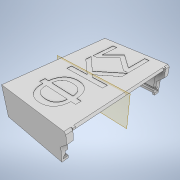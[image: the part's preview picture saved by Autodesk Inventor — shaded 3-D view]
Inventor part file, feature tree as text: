
AUTODESK INVENTOR PART (.ipt)
format: ipt  version: 2020.1 (Build 241239000, 239)  size: 393,728 bytes
history: native  units: mm
features: extrude x12, sketch x12, mirror x4, projected_geometry x3, chamfer x2, plane x1
ambient origin geometry x8: Origin, YZ Plane, XZ Plane, XY Plane, X Axis, Y Axis, Z Axis, Center Point
bodies: Solid1 (feature_tree)
feature tree (34):
  extrude  "Extrusion1"  Depth=100.0mm
  extrude  "Extrusion2"  Depth=1.5mm
  extrude  "Extrusion3"  Depth=20.868mm
  plane  "Work Plane1"
  mirror  "Mirror1"
  extrude  "Extrusion5"  TaperAngle=135.0deg  [1 undecoded]
  extrude  "Extrusion6"  TaperAngle=0.0deg  [1 undecoded]
  mirror  "Mirror3"
  extrude  "Extrusion8"  Depth=5.419mm
  chamfer  "Chamfer1"  Distance=2.0mm
  extrude  "Extrusion9"  Depth=15.0mm
  chamfer  "Chamfer4"  Distance=0.25mm
  extrude  "Extrusion10"  Depth=1.5mm
  extrude  "Extrusion11"  Depth=1.5mm
  extrude  "Extrusion12"  Depth=1.5mm TaperAngle=0.0deg
  mirror  "Mirror4"
  extrude  "Extrusion13"  Depth=2.0mm TaperAngle=45.0deg
  extrude  "Extrusion14"  TaperAngle=90.0deg  [1 undecoded]
  mirror  "Mirror5"
  sketch  "Sketch1"  dims[d0=63.837mm d1=100.0mm]
  sketch  "Sketch2"  dims[d2=1.5mm d3=0.0mm d4=3.0mm]
  sketch  "Sketch3"  dims[d5=25.0mm d6=0.0mm d7=20.868mm]
  sketch  "Sketch7"  dims[d8=2.828427mm d9=135.0deg]
  projected_geometry  "Projected Loop2"
  projected_geometry  "Projected Loop3"
  sketch  "Sketch8"  dims[d10=1.0mm d11=0.0mm d12=0.0mm]
  sketch  "Sketch10"  dims[d22=1.0mm d23=0.0mm d24=5.419mm]
  sketch  "Sketch11"  dims[d26=0.0mm d27=2.0mm d28=0.0mm]
  sketch  "Sketch12"  dims[d31=3.0mm d32=0.0mm d33=15.0mm]
  projected_geometry  "Projected Loop5"
  sketch  "Sketch13"  dims[d34=15.0mm]
  sketch  "Sketch14"  dims[d35=30.0mm]
  sketch  "Sketch15"  dims[d36=30.0mm d37=0.25mm d38=0.0mm]
  sketch  "Sketch16"  dims[d39=1.5mm d40=2.0mm d41=45.0deg d48=5.418mm d49=13.0mm d50=10.0mm d51=0.0mm d52=5.418mm d53=2.0mm d54=45.0deg d55=90.0deg d56=2.0mm d57=0.0mm d58=2.0mm d60=2.0mm d61=0.0mm d62=2.25mm d63=10.0mm d64=0.0mm d65=10.0mm d66=0.0mm d67=2.0mm d68=5.0mm d69=1.5mm d70=0.0mm]
note: 3 required parameter values undecoded (feature->parameter linkage not recoverable at this tier; creation-order binding heuristic only, values carry confidence <= 0.55)
